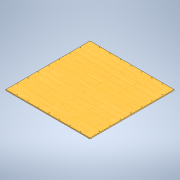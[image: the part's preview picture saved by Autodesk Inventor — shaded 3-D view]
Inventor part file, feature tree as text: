
AUTODESK INVENTOR PART (.ipt)
format: ipt  version: 2021.3 (Build 253353000, 353)  size: 217,088 bytes
history: native  units: mm
features: sketch x1, extrude x1
ambient origin geometry x8: Origin, YZ Plane, XZ Plane, XY Plane, X Axis, Y Axis, Z Axis, Center Point
bodies: Solid1 (feature_tree)
feature tree (2):
  sketch  "Sketch1"  dims[d0=700.0mm d1=700.0mm d2=21.0mm d3=21.0mm d4=40.0mm d6=360.0deg d8=21.0mm d9=99.0mm d10=141.0mm d11=8.0mm d12=0.0mm d13=10.0mm d14=4.0mm d15=4.0mm d16=4.0mm d17=175.0mm d18=87.5mm d19=87.5mm d20=4.0mm d21=40.0mm d23=360.0deg d25=130.0mm d26=120.0mm d27=60.0mm d28=140.0mm d29=25.0mm d30=50.0mm]
  extrude  "Extrusion1"  Depth=700.0mm
